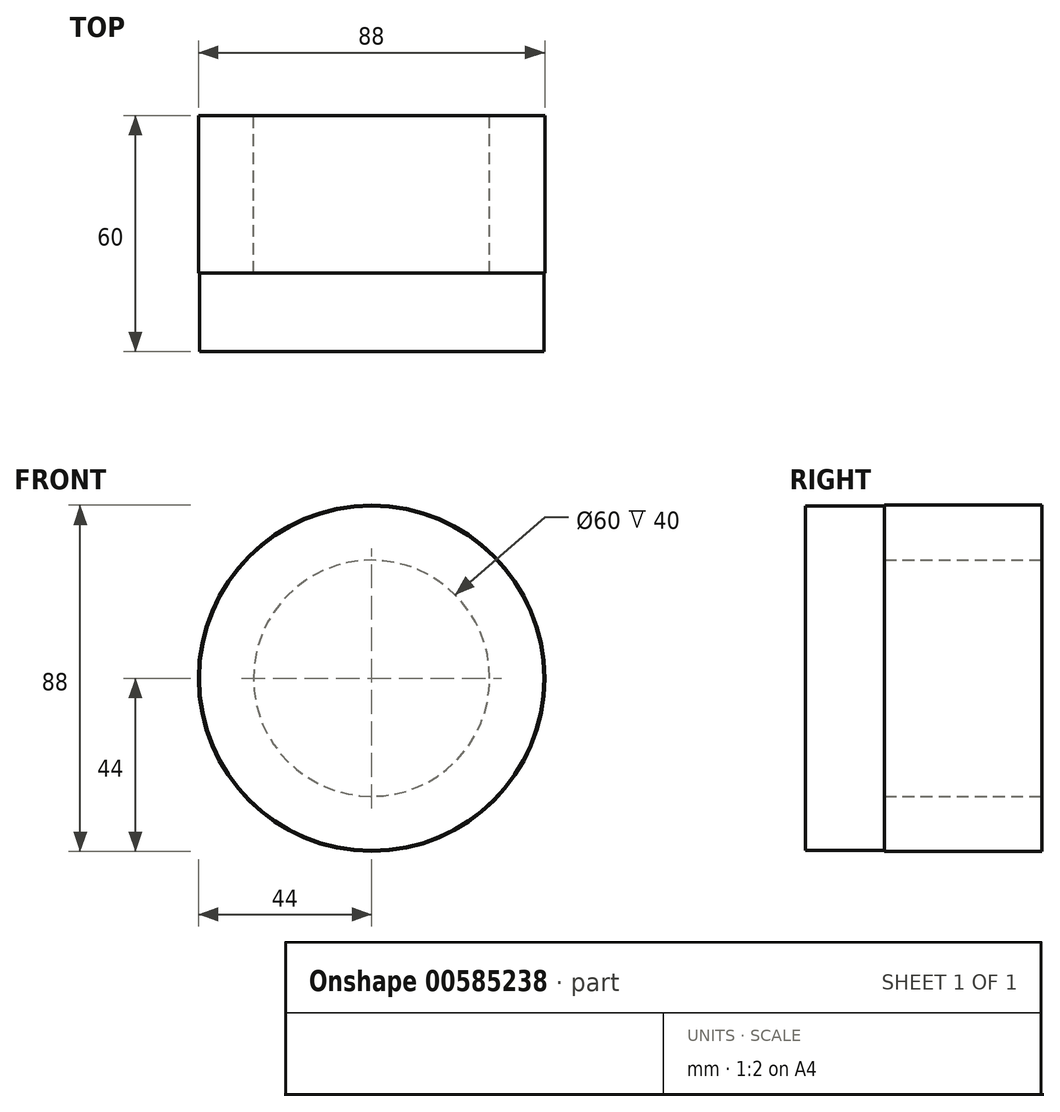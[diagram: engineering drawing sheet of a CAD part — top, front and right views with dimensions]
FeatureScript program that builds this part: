
annotation { "Feature Type Name" : "Feature", "Feature Type Description" : "" }
export const myFeature = defineFeature(function(context is Context, id is Id, definition is map)
    precondition{}
    {
        {
            var Q0;
            Q0=qCreatedBy(makeId("Front.planeOp"),FACE);
            var sketch = newSketch(context, id + "F0", { "sketchPlane" : qUnion([Q0])});
            skCircle(sketch, "E0", {"center": v(0, 0) * mm, "radius": 30 * mm});
            skCircle(sketch, "E1", {"center": v(0, 0) * mm, "radius": 44 * mm});
            skSolve(sketch);
        }
        {
            var Q0;
            Q0 = qSketchRegion(id + "F0", true);
            extrude(context, id + "F1", {"entities" : qUnion([Q0]), "depth" : 60 * mm, "offsetDistance" : 25 * mm, "hasSecondDirection" : true, "secondDirectionOppositeDirection" : true, "secondDirectionDepth" : -20 * mm});
        }
        {
            var Q0;
            Q0=qCreatedBy(makeId("Front.planeOp"),FACE);
            var sketch = newSketch(context, id + "F2", { "sketchPlane" : qUnion([Q0])});
            skCircle(sketch, "E2", {"center": v(0, 0) * mm, "radius": 43.76 * mm});
            skSolve(sketch);
        }
        {
            var Q0;
            Q0 = qSketchRegion(id + "F2", true);
            extrude(context, id + "F3", {"entities" : qUnion([Q0]), "operationType" : NewBodyOperationType.ADD, "depth" : 80 * mm, "offsetDistance" : 25 * mm, "hasSecondDirection" : true, "secondDirectionOppositeDirection" : false, "secondDirectionDepth" : 60 * mm});
        }
    });
